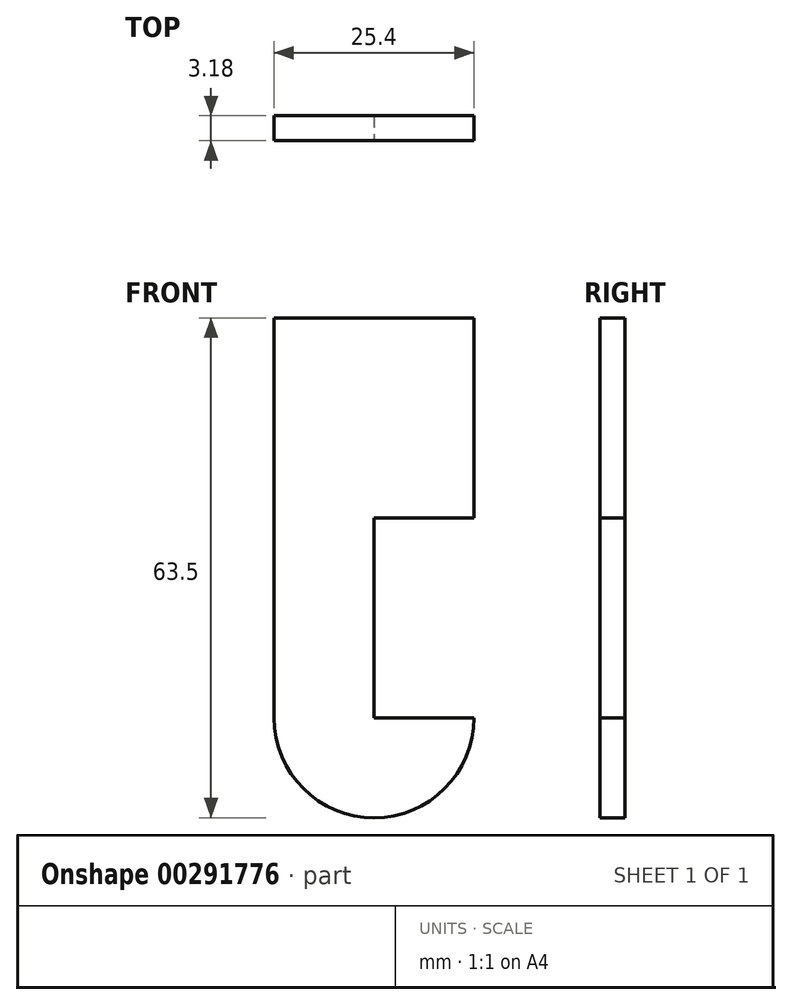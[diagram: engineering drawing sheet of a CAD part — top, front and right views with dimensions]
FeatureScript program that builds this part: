
annotation { "Feature Type Name" : "Feature", "Feature Type Description" : "" }
export const myFeature = defineFeature(function(context is Context, id is Id, definition is map)
    precondition{}
    {
        {
            var Q0;
            Q0=qCreatedBy(makeId("Front.planeOp"),FACE);
            var sketch = newSketch(context, id + "F0", { "sketchPlane" : qUnion([Q0])});
            skLineSegment(sketch, "E0.bottom", {"start": v(-13.03, 52.74) * mm, "end": v(12.37, 52.74) * mm});
            skLineSegment(sketch, "E0.top", {"start": v(-13.03, 27.34) * mm, "end": v(12.37, 27.34) * mm});
            skLineSegment(sketch, "E0.left", {"start": v(-13.03, 52.74) * mm, "end": v(-13.03, 27.34) * mm});
            skLineSegment(sketch, "E0.right", {"start": v(12.37, 52.74) * mm, "end": v(12.37, 27.34) * mm});
            skSolve(sketch);
        }
        {
            var Q0;
            Q0 = qSketchRegion(id + "F0", true);
            extrude(context, id + "F1", {"entities" : qUnion([Q0]), "endBound" : BoundingType.SYMMETRIC, "depth" : 3.17 * mm});
        }
        {
            var Q0;
            Q0=makeQuery(id+"F1.opExtrude","CAP_FACE",FACE,{"disambiguationData":[OSD([sQuery(id+"F0.wireOp",EDGE,"E0.bottom"),sQuery(id+"F0.wireOp",EDGE,"E0.top"),sQuery(id+"F0.wireOp",EDGE,"E0.left"),sQuery(id+"F0.wireOp",EDGE,"E0.right")])],"isStart":false});
            var sketch = newSketch(context, id + "F2", { "sketchPlane" : qUnion([Q0])});
            skPoint(sketch, "E1.oppositeSnap0", {"position": v(-0.33, 27.34) * mm});
            skLineSegment(sketch, "E1.bottom", {"start": v(-13.03, 27.34) * mm, "end": v(-0.33, 27.34) * mm});
            skLineSegment(sketch, "E1.top", {"start": v(-13.03, 1.94) * mm, "end": v(-0.33, 1.94) * mm});
            skLineSegment(sketch, "E1.left", {"start": v(-13.03, 27.34) * mm, "end": v(-13.03, 1.94) * mm});
            skLineSegment(sketch, "E1.right", {"start": v(-0.33, 27.34) * mm, "end": v(-0.33, 1.94) * mm});
            skSolve(sketch);
        }
        {
            var Q0;
            Q0 = qSketchRegion(id + "F2", true);
            extrude(context, id + "F3", {"entities" : qUnion([Q0]), "operationType" : NewBodyOperationType.ADD, "oppositeDirection" : true, "depth" : 3.17 * mm});
        }
        {
            var Q0;
            Q0=makeQuery(id+"F3.boolean.opBoolean","MERGE",FACE,{"derivedFrom":[makeQuery(id+"F1.opExtrude","CAP_FACE",FACE,{"disambiguationData":[OSD([sQuery(id+"F0.wireOp",EDGE,"E0.bottom"),sQuery(id+"F0.wireOp",EDGE,"E0.top"),sQuery(id+"F0.wireOp",EDGE,"E0.left"),sQuery(id+"F0.wireOp",EDGE,"E0.right")])],"isStart":false}),makeQuery(id+"F3.opExtrude","CAP_FACE",FACE,{"disambiguationData":[OSD([sQuery(id+"F2.wireOp",EDGE,"E1.bottom"),sQuery(id+"F2.wireOp",EDGE,"E1.top"),sQuery(id+"F2.wireOp",EDGE,"E1.left"),sQuery(id+"F2.wireOp",EDGE,"E1.right")])],"isStart":true})]});
            var sketch = newSketch(context, id + "F4", { "sketchPlane" : qUnion([Q0])});
            skArc(sketch, "E2", {"start": v(-13.03, 1.94) * mm, "mid": v(-0.33, -10.76) * mm, "end": v(12.37, 1.94) * mm});
            skLineSegment(sketch, "E3", {"start": v(12.37, 1.94) * mm, "end": v(-13.03, 1.94) * mm, "construction": true});
            skLineSegment(sketch, "E4", {"start": v(-13.03, 1.94) * mm, "end": v(12.37, 1.94) * mm});
            skSolve(sketch);
        }
        {
            var Q0;
            Q0 = qSketchRegion(id + "F4", true);
            extrude(context, id + "F5", {"entities" : qUnion([Q0]), "operationType" : NewBodyOperationType.ADD, "oppositeDirection" : true, "depth" : 3.17 * mm});
        }
    });
